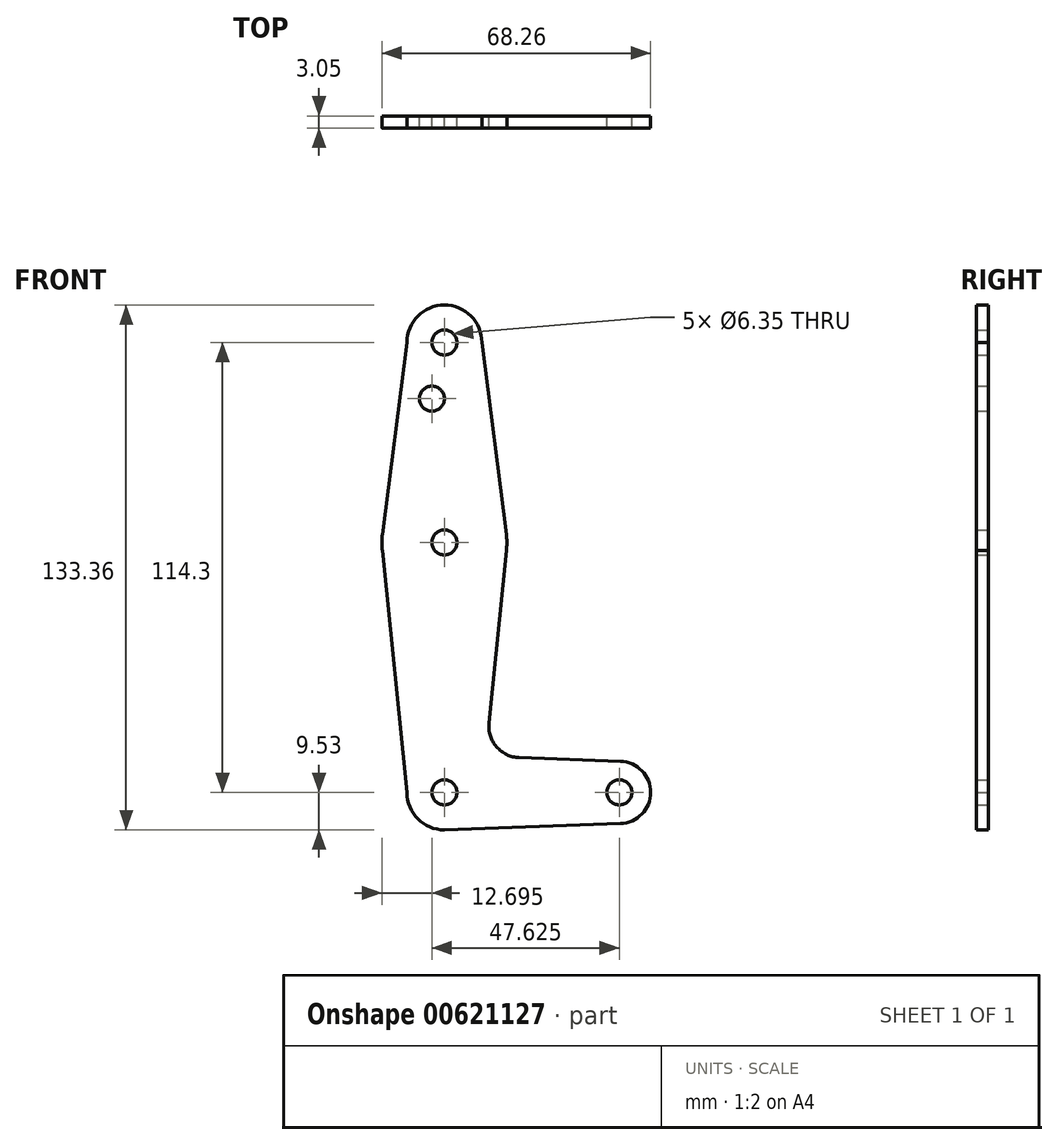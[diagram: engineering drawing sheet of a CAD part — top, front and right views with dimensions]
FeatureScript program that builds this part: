
annotation { "Feature Type Name" : "Feature", "Feature Type Description" : "" }
export const myFeature = defineFeature(function(context is Context, id is Id, definition is map)
    precondition{}
    {
        {
            var Q0;
            Q0=qCreatedBy(makeId("Front.planeOp"),FACE);
            var sketch = newSketch(context, id + "F0", { "sketchPlane" : qUnion([Q0])});
            skLineSegment(sketch, "E0", {"start": v(0, 0) * mm, "end": v(0, 114.3) * mm});
            skLineSegment(sketch, "E1", {"start": v(0, 0) * mm, "end": v(44.45, 0) * mm});
            skCircle(sketch, "E2", {"center": v(0, 114.3) * mm, "radius": 9.52 * mm});
            skCircle(sketch, "E3", {"center": v(0, 0) * mm, "radius": 9.53 * mm});
            skCircle(sketch, "E4", {"center": v(44.45, 0) * mm, "radius": 7.94 * mm});
            skCircle(sketch, "E5", {"center": v(0, 63.5) * mm, "radius": 15.88 * mm});
            skLineSegment(sketch, "E6", {"start": v(-9.52, 114.3) * mm, "end": v(-15.75, 65.5) * mm});
            skLineSegment(sketch, "E7", {"start": v(-15.75, 65.5) * mm, "end": v(-15.75, 61.5) * mm});
            skLineSegment(sketch, "E8", {"start": v(0, -9.52) * mm, "end": v(44.73, -7.93) * mm});
            skLineSegment(sketch, "E9.MirrorCS", {"start": v(9.52, 114.3) * mm, "end": v(15.75, 65.5) * mm});
            skLineSegment(sketch, "E10.MirrorCS", {"start": v(15.75, 61.5) * mm, "end": v(11.34, 17.59) * mm});
            skLineSegment(sketch, "E11.MirrorCS", {"start": v(18.97, 8.85) * mm, "end": v(44.73, 7.93) * mm});
            skCircle(sketch, "E12", {"center": v(0, 114.3) * mm, "radius": 3.18 * mm});
            skCircle(sketch, "E13", {"center": v(-3.18, 100.03) * mm, "radius": 3.18 * mm});
            skCircle(sketch, "E14", {"center": v(0, 63.5) * mm, "radius": 3.18 * mm});
            skCircle(sketch, "E15", {"center": v(0, 0) * mm, "radius": 3.18 * mm});
            skCircle(sketch, "E16", {"center": v(44.45, 0) * mm, "radius": 3.18 * mm});
            skPoint(sketch, "E17.newPointA", {"position": v(9.57, 0) * mm});
            skPoint(sketch, "E17.newPointB", {"position": v(0, 9.53) * mm});
            skArc(sketch, "E17.filletArc", {"start": v(11.34, 17.59) * mm, "mid": v(13.26, 11.57) * mm, "end": v(18.97, 8.85) * mm});
            skLineSegment(sketch, "E18", {"start": v(-9.53, 0) * mm, "end": v(-15.75, 61.5) * mm});
            skSolve(sketch);
        }
        {
            var Q0;
            {var subQ0=sQuery(id+"F0.wireOp",EDGE,"E7");Q0=makeQuery(id+"F0.imprint","IMPRINT",FACE,{"disambiguationData":[TD([[makeQuery(id+"F0.imprint","IMPRINT",EDGE,{"derivedFrom":subQ0}),-1.0]])]});}
            var Q1;
            {var subQ5=sQuery(id+"F0.wireOp",EDGE,"E18");Q1=makeQuery(id+"F0.imprint","IMPRINT",FACE,{"disambiguationData":[TD([[makeQuery(id+"F0.imprint","IMPRINT",EDGE,{"derivedFrom":subQ5}),-1.0]])]});}
            var Q2;
            {var subQ10=sQuery(id+"F0.wireOp",EDGE,"E10.MirrorCS");Q2=makeQuery(id+"F0.imprint","IMPRINT",FACE,{"disambiguationData":[TD([[makeQuery(id+"F0.imprint","IMPRINT",EDGE,{"derivedFrom":subQ10}),-1.0]])]});}
            var Q3;
            {var subQ0=sQuery(id+"F0.wireOp",EDGE,"E5");var subQ2=sQuery(id+"F0.wireOp",EDGE,"E0");var subQ3=makeQuery(id+"F0.imprint","INTERSECT",VERTEX,{"disambiguationData":[OD(0.0)],"derivedFrom":[subQ2,subQ0]});Q3=makeQuery(id+"F0.imprint","IMPRINT",FACE,{"disambiguationData":[TD([[makeQuery(id+"F0.imprint","IMPRINT",EDGE,{"disambiguationData":[TD([[subQ3,-1.0]])],"derivedFrom":subQ2}),-1.0]])]});}
            var Q4;
            {var subQ0=sQuery(id+"F0.wireOp",EDGE,"E7");Q4=makeQuery(id+"F0.imprint","IMPRINT",FACE,{"disambiguationData":[TD([[makeQuery(id+"F0.imprint","IMPRINT",EDGE,{"derivedFrom":subQ0}),1.0]])]});}
            var Q5;
            {var subQ0=sQuery(id+"F0.wireOp",EDGE,"E6");Q5=makeQuery(id+"F0.imprint","IMPRINT",FACE,{"disambiguationData":[TD([[makeQuery(id+"F0.imprint","IMPRINT",EDGE,{"derivedFrom":subQ0}),1.0]])]});}
            var Q6;
            {var subQ0=sQuery(id+"F0.wireOp",EDGE,"E9.MirrorCS");Q6=makeQuery(id+"F0.imprint","IMPRINT",FACE,{"disambiguationData":[TD([[makeQuery(id+"F0.imprint","IMPRINT",EDGE,{"derivedFrom":subQ0}),-1.0]])]});}
            var Q7;
            {var subQ2=sQuery(id+"F0.wireOp",EDGE,"E0");var subQ4=sQuery(id+"F0.wireOp",EDGE,"E15");var subQ10=makeQuery(id+"F0.imprint","INTERSECT",VERTEX,{"derivedFrom":[subQ2,subQ4]});Q7=makeQuery(id+"F0.imprint","IMPRINT",FACE,{"disambiguationData":[TD([[makeQuery(id+"F0.imprint","IMPRINT",EDGE,{"disambiguationData":[TD([[subQ10,-1.0]])],"derivedFrom":subQ2}),1.0]])]});}
            var Q8;
            {var subQ0=sQuery(id+"F0.wireOp",EDGE,"E4");var subQ1=sQuery(id+"F0.wireOp",EDGE,"E1");var subQ2=makeQuery(id+"F0.imprint","INTERSECT",VERTEX,{"derivedFrom":[subQ1,subQ0]});Q8=makeQuery(id+"F0.imprint","IMPRINT",FACE,{"disambiguationData":[TD([[makeQuery(id+"F0.imprint","IMPRINT",EDGE,{"disambiguationData":[TD([[subQ2,1.0]])],"derivedFrom":subQ1}),-1.0]])]});}
            var Q9;
            Q9=makeQuery(id+"F0.imprint","IMPRINT",FACE,{"disambiguationData":[TD([[makeQuery(id+"F0.imprint","IMPRINT",EDGE,{"derivedFrom":sQuery(id+"F0.wireOp",EDGE,"E16")}),-1.0]])]});
            var Q10;
            Q10=makeQuery(id+"F0.imprint","IMPRINT",FACE,{"disambiguationData":[TD([[makeQuery(id+"F0.imprint","IMPRINT",EDGE,{"derivedFrom":sQuery(id+"F0.wireOp",EDGE,"E16")}),-1.0]])]});
            var Q11;
            Q11=makeQuery(id+"F0.imprint","IMPRINT",FACE,{"disambiguationData":[TD([[makeQuery(id+"F0.imprint","IMPRINT",EDGE,{"derivedFrom":sQuery(id+"F0.wireOp",EDGE,"E12")}),-1.0]])]});
            var Q12;
            {var subQ0=sQuery(id+"F0.wireOp",EDGE,"E15");var subQ1=sQuery(id+"F0.wireOp",EDGE,"E0");var subQ2=makeQuery(id+"F0.imprint","INTERSECT",VERTEX,{"derivedFrom":[subQ1,subQ0]});Q12=makeQuery(id+"F0.imprint","IMPRINT",FACE,{"disambiguationData":[TD([[makeQuery(id+"F0.imprint","IMPRINT",EDGE,{"disambiguationData":[TD([[subQ2,-1.0]])],"derivedFrom":subQ1}),-1.0]])]});}
            var Q13;
            {var subQ0=sQuery(id+"F0.wireOp",EDGE,"E15");var subQ1=sQuery(id+"F0.wireOp",EDGE,"E0");var subQ2=makeQuery(id+"F0.imprint","INTERSECT",VERTEX,{"derivedFrom":[subQ1,subQ0]});Q13=makeQuery(id+"F0.imprint","IMPRINT",FACE,{"disambiguationData":[TD([[makeQuery(id+"F0.imprint","IMPRINT",EDGE,{"disambiguationData":[TD([[subQ2,-1.0]])],"derivedFrom":subQ1}),-1.0]])]});}
            extrude(context, id + "F1", {"entities" : qUnion([Q0, Q1, Q2, Q3, Q4, Q5, Q6, Q7, Q8, Q9, Q10, Q11, Q12, Q13]), "depth" : 3.05 * mm, "offsetDistance" : 25.4 * mm});
        }
    });
